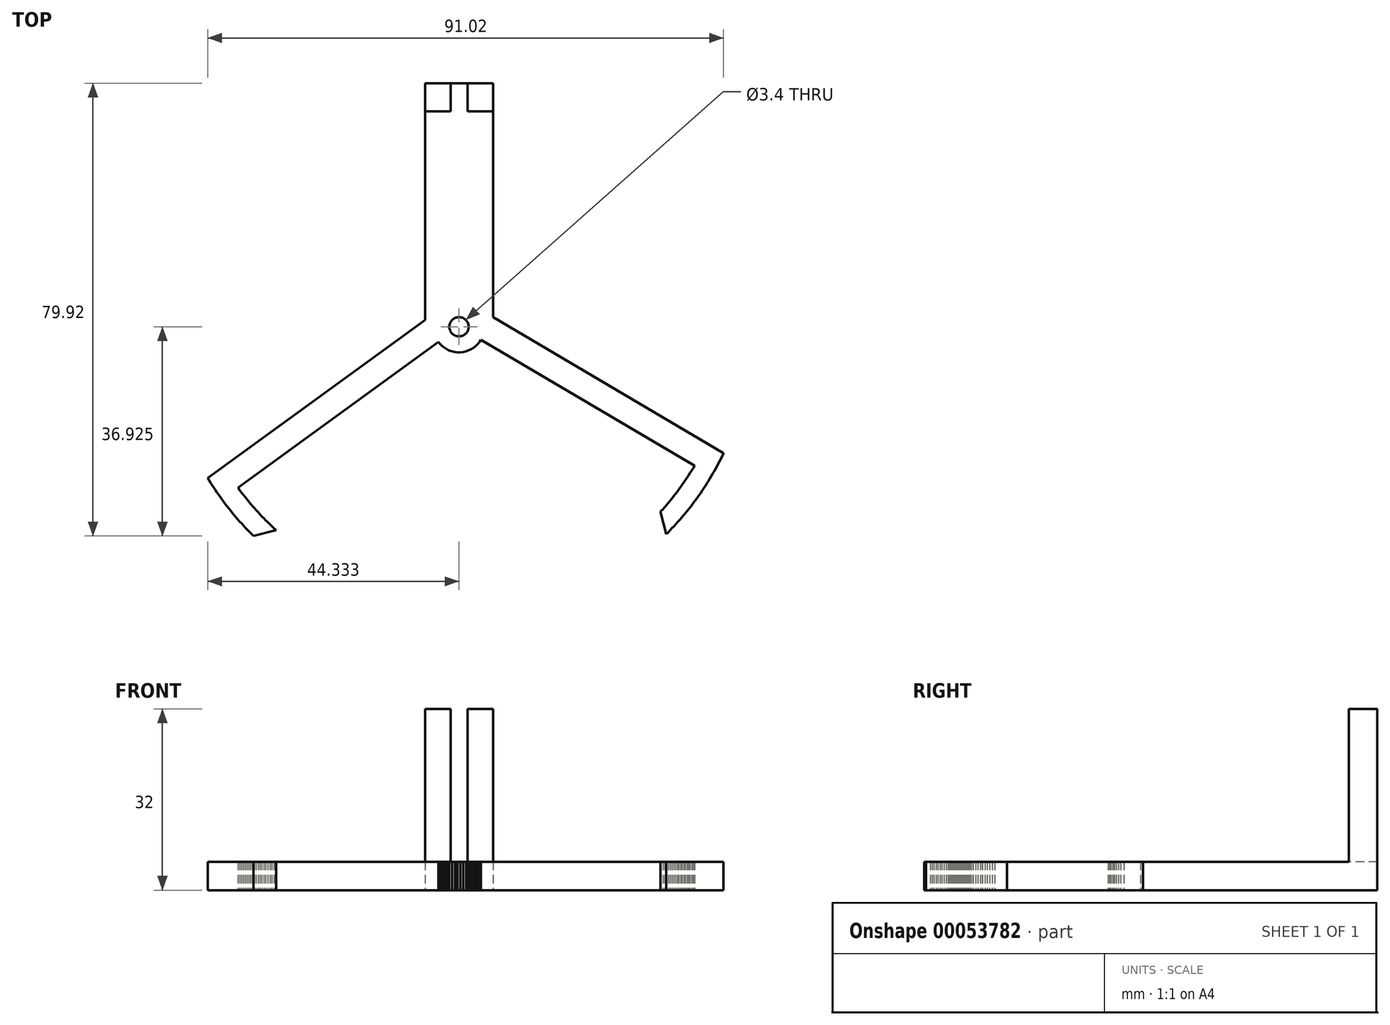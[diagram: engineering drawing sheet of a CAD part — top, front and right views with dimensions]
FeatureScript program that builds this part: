
annotation { "Feature Type Name" : "Feature", "Feature Type Description" : "" }
export const myFeature = defineFeature(function(context is Context, id is Id, definition is map)
    precondition{}
    {
        {
            var Q0;
            Q0=qCreatedBy(makeId("Top.planeOp"),FACE);
            var sketch = newSketch(context, id + "F0", { "sketchPlane" : qUnion([Q0])});
            skLineSegment(sketch, "E0", {"start": v(-33.44, -19.66) * mm, "end": v(-33.81, -19.33) * mm});
            skLineSegment(sketch, "E1", {"start": v(-33.81, -19.33) * mm, "end": v(-34.18, -18.99) * mm});
            skLineSegment(sketch, "E2", {"start": v(-34.18, -18.99) * mm, "end": v(-34.54, -18.64) * mm});
            skLineSegment(sketch, "E3", {"start": v(-34.54, -18.64) * mm, "end": v(-34.9, -18.3) * mm});
            skLineSegment(sketch, "E4", {"start": v(-34.9, -18.3) * mm, "end": v(-35.26, -17.95) * mm});
            skLineSegment(sketch, "E5", {"start": v(-35.26, -17.95) * mm, "end": v(-35.61, -17.6) * mm});
            skLineSegment(sketch, "E6", {"start": v(-35.61, -17.6) * mm, "end": v(-35.96, -17.23) * mm});
            skLineSegment(sketch, "E7", {"start": v(-35.96, -17.23) * mm, "end": v(-36.3, -16.87) * mm});
            skLineSegment(sketch, "E8", {"start": v(-36.3, -16.87) * mm, "end": v(-36.65, -16.5) * mm});
            skLineSegment(sketch, "E9", {"start": v(-36.65, -16.5) * mm, "end": v(-36.98, -16.13) * mm});
            skLineSegment(sketch, "E10", {"start": v(-36.98, -16.13) * mm, "end": v(-37.32, -15.76) * mm});
            skLineSegment(sketch, "E11", {"start": v(-37.32, -15.76) * mm, "end": v(-37.65, -15.39) * mm});
            skLineSegment(sketch, "E12", {"start": v(-37.65, -15.39) * mm, "end": v(-37.97, -15) * mm});
            skLineSegment(sketch, "E13", {"start": v(-37.97, -15) * mm, "end": v(-38.3, -14.62) * mm});
            skLineSegment(sketch, "E14", {"start": v(-38.3, -14.62) * mm, "end": v(-38.6, -14.24) * mm});
            skLineSegment(sketch, "E15", {"start": v(-38.6, -14.24) * mm, "end": v(-38.92, -13.85) * mm});
            skLineSegment(sketch, "E16", {"start": v(-38.92, -13.85) * mm, "end": v(-39.23, -13.45) * mm});
            skLineSegment(sketch, "E17", {"start": v(-39.23, -13.45) * mm, "end": v(-39.54, -13.06) * mm});
            skLineSegment(sketch, "E18", {"start": v(-39.54, -13.06) * mm, "end": v(-39.84, -12.66) * mm});
            skLineSegment(sketch, "E19", {"start": v(-39.84, -12.66) * mm, "end": v(-40.14, -12.26) * mm});
            skLineSegment(sketch, "E20", {"start": v(-40.14, -12.26) * mm, "end": v(-40.2, -12.17) * mm});
            skLineSegment(sketch, "E21", {"start": v(-40.2, -12.17) * mm, "end": v(-4.82, 13.57) * mm});
            skLineSegment(sketch, "E22", {"start": v(-4.82, 13.57) * mm, "end": v(-4.5, 13.18) * mm});
            skLineSegment(sketch, "E23", {"start": v(-4.5, 13.18) * mm, "end": v(-4.14, 12.83) * mm});
            skLineSegment(sketch, "E24", {"start": v(-4.14, 12.83) * mm, "end": v(-3.75, 12.52) * mm});
            skLineSegment(sketch, "E25", {"start": v(-3.75, 12.52) * mm, "end": v(-3.32, 12.26) * mm});
            skLineSegment(sketch, "E26", {"start": v(-3.32, 12.26) * mm, "end": v(-2.87, 12.05) * mm});
            skLineSegment(sketch, "E27", {"start": v(-2.87, 12.05) * mm, "end": v(-2.4, 11.88) * mm});
            skLineSegment(sketch, "E28", {"start": v(-2.4, 11.88) * mm, "end": v(-1.91, 11.78) * mm});
            skLineSegment(sketch, "E29", {"start": v(-1.91, 11.78) * mm, "end": v(-1.42, 11.72) * mm});
            skLineSegment(sketch, "E30", {"start": v(-1.42, 11.72) * mm, "end": v(-0.92, 11.72) * mm});
            skLineSegment(sketch, "E31", {"start": v(-0.92, 11.72) * mm, "end": v(-0.42, 11.78) * mm});
            skLineSegment(sketch, "E32", {"start": v(-0.42, 11.78) * mm, "end": v(0.07, 11.9) * mm});
            skLineSegment(sketch, "E33", {"start": v(0.07, 11.9) * mm, "end": v(0.54, 12.06) * mm});
            skLineSegment(sketch, "E34", {"start": v(0.54, 12.06) * mm, "end": v(1, 12.27) * mm});
            skLineSegment(sketch, "E35", {"start": v(1, 12.27) * mm, "end": v(1.41, 12.54) * mm});
            skLineSegment(sketch, "E36", {"start": v(1.41, 12.54) * mm, "end": v(1.8, 12.85) * mm});
            skLineSegment(sketch, "E37", {"start": v(1.8, 12.85) * mm, "end": v(2.16, 13.2) * mm});
            skLineSegment(sketch, "E38", {"start": v(2.16, 13.2) * mm, "end": v(2.48, 13.59) * mm});
            skLineSegment(sketch, "E39", {"start": v(2.48, 13.59) * mm, "end": v(2.7, 13.93) * mm});
            skLineSegment(sketch, "E40", {"start": v(2.7, 13.93) * mm, "end": v(40.39, -8.3) * mm});
            skLineSegment(sketch, "E41", {"start": v(40.39, -8.3) * mm, "end": v(40.13, -8.73) * mm});
            skLineSegment(sketch, "E42", {"start": v(40.13, -8.73) * mm, "end": v(39.87, -9.16) * mm});
            skLineSegment(sketch, "E43", {"start": v(39.87, -9.16) * mm, "end": v(39.6, -9.58) * mm});
            skLineSegment(sketch, "E44", {"start": v(39.6, -9.58) * mm, "end": v(39.34, -10) * mm});
            skLineSegment(sketch, "E45", {"start": v(39.34, -10) * mm, "end": v(39.06, -10.42) * mm});
            skLineSegment(sketch, "E46", {"start": v(39.06, -10.42) * mm, "end": v(38.78, -10.84) * mm});
            skLineSegment(sketch, "E47", {"start": v(38.78, -10.84) * mm, "end": v(38.5, -11.25) * mm});
            skLineSegment(sketch, "E48", {"start": v(38.5, -11.25) * mm, "end": v(38.21, -11.66) * mm});
            skLineSegment(sketch, "E49", {"start": v(38.21, -11.66) * mm, "end": v(37.92, -12.06) * mm});
            skLineSegment(sketch, "E50", {"start": v(37.92, -12.06) * mm, "end": v(37.63, -12.47) * mm});
            skLineSegment(sketch, "E51", {"start": v(37.63, -12.47) * mm, "end": v(37.33, -12.87) * mm});
            skLineSegment(sketch, "E52", {"start": v(37.33, -12.87) * mm, "end": v(37.03, -13.27) * mm});
            skLineSegment(sketch, "E53", {"start": v(37.03, -13.27) * mm, "end": v(36.72, -13.66) * mm});
            skLineSegment(sketch, "E54", {"start": v(36.72, -13.66) * mm, "end": v(36.4, -14.05) * mm});
            skLineSegment(sketch, "E55", {"start": v(36.4, -14.05) * mm, "end": v(36.1, -14.44) * mm});
            skLineSegment(sketch, "E56", {"start": v(36.1, -14.44) * mm, "end": v(35.77, -14.82) * mm});
            skLineSegment(sketch, "E57", {"start": v(35.77, -14.82) * mm, "end": v(35.45, -15.2) * mm});
            skLineSegment(sketch, "E58", {"start": v(35.45, -15.2) * mm, "end": v(35.12, -15.58) * mm});
            skLineSegment(sketch, "E59", {"start": v(35.12, -15.58) * mm, "end": v(34.79, -15.96) * mm});
            skLineSegment(sketch, "E60", {"start": v(34.79, -15.96) * mm, "end": v(34.45, -16.33) * mm});
            skLineSegment(sketch, "E61", {"start": v(34.45, -16.33) * mm, "end": v(34.38, -16.4) * mm});
            skLineSegment(sketch, "E62", {"start": v(34.38, -16.4) * mm, "end": v(35.4, -20.4) * mm});
            skLineSegment(sketch, "E63", {"start": v(35.4, -20.4) * mm, "end": v(35.74, -20.04) * mm});
            skLineSegment(sketch, "E64", {"start": v(35.74, -20.04) * mm, "end": v(36.1, -19.68) * mm});
            skLineSegment(sketch, "E65", {"start": v(36.1, -19.68) * mm, "end": v(36.44, -19.32) * mm});
            skLineSegment(sketch, "E66", {"start": v(36.44, -19.32) * mm, "end": v(36.78, -18.96) * mm});
            skLineSegment(sketch, "E67", {"start": v(36.78, -18.96) * mm, "end": v(37.12, -18.59) * mm});
            skLineSegment(sketch, "E68", {"start": v(37.12, -18.59) * mm, "end": v(37.45, -18.22) * mm});
            skLineSegment(sketch, "E69", {"start": v(37.45, -18.22) * mm, "end": v(37.78, -17.84) * mm});
            skLineSegment(sketch, "E70", {"start": v(37.78, -17.84) * mm, "end": v(38.1, -17.46) * mm});
            skLineSegment(sketch, "E71", {"start": v(38.1, -17.46) * mm, "end": v(38.43, -17.08) * mm});
            skLineSegment(sketch, "E72", {"start": v(38.43, -17.08) * mm, "end": v(38.75, -16.7) * mm});
            skLineSegment(sketch, "E73", {"start": v(38.75, -16.7) * mm, "end": v(39.07, -16.3) * mm});
            skLineSegment(sketch, "E74", {"start": v(39.07, -16.3) * mm, "end": v(39.38, -15.92) * mm});
            skLineSegment(sketch, "E75", {"start": v(39.38, -15.92) * mm, "end": v(39.69, -15.53) * mm});
            skLineSegment(sketch, "E76", {"start": v(39.69, -15.53) * mm, "end": v(40, -15.13) * mm});
            skLineSegment(sketch, "E77", {"start": v(40, -15.13) * mm, "end": v(40.3, -14.73) * mm});
            skLineSegment(sketch, "E78", {"start": v(40.3, -14.73) * mm, "end": v(40.6, -14.33) * mm});
            skLineSegment(sketch, "E79", {"start": v(40.6, -14.33) * mm, "end": v(40.89, -13.92) * mm});
            skLineSegment(sketch, "E80", {"start": v(40.89, -13.92) * mm, "end": v(41.17, -13.52) * mm});
            skLineSegment(sketch, "E81", {"start": v(41.17, -13.52) * mm, "end": v(41.46, -13.1) * mm});
            skLineSegment(sketch, "E82", {"start": v(41.46, -13.1) * mm, "end": v(41.74, -12.7) * mm});
            skLineSegment(sketch, "E83", {"start": v(41.74, -12.7) * mm, "end": v(42.02, -12.28) * mm});
            skLineSegment(sketch, "E84", {"start": v(42.02, -12.28) * mm, "end": v(42.3, -11.86) * mm});
            skLineSegment(sketch, "E85", {"start": v(42.3, -11.86) * mm, "end": v(42.56, -11.44) * mm});
            skLineSegment(sketch, "E86", {"start": v(42.56, -11.44) * mm, "end": v(42.83, -11.01) * mm});
            skLineSegment(sketch, "E87", {"start": v(42.83, -11.01) * mm, "end": v(43.09, -10.58) * mm});
            skLineSegment(sketch, "E88", {"start": v(43.09, -10.58) * mm, "end": v(43.34, -10.16) * mm});
            skLineSegment(sketch, "E89", {"start": v(43.34, -10.16) * mm, "end": v(43.6, -9.72) * mm});
            skLineSegment(sketch, "E90", {"start": v(43.6, -9.72) * mm, "end": v(43.85, -9.3) * mm});
            skLineSegment(sketch, "E91", {"start": v(43.85, -9.3) * mm, "end": v(44.09, -8.85) * mm});
            skLineSegment(sketch, "E92", {"start": v(44.09, -8.85) * mm, "end": v(44.33, -8.42) * mm});
            skLineSegment(sketch, "E93", {"start": v(44.33, -8.42) * mm, "end": v(44.57, -7.98) * mm});
            skLineSegment(sketch, "E94", {"start": v(44.57, -7.98) * mm, "end": v(44.8, -7.53) * mm});
            skLineSegment(sketch, "E95", {"start": v(44.8, -7.53) * mm, "end": v(45.02, -7.09) * mm});
            skLineSegment(sketch, "E96", {"start": v(45.02, -7.09) * mm, "end": v(45.25, -6.64) * mm});
            skLineSegment(sketch, "E97", {"start": v(45.25, -6.64) * mm, "end": v(45.47, -6.19) * mm});
            skLineSegment(sketch, "E98", {"start": v(45.47, -6.19) * mm, "end": v(45.51, -6.1) * mm});
            skLineSegment(sketch, "E99", {"start": v(45.51, -6.1) * mm, "end": v(1.1, 20.1) * mm});
            skLineSegment(sketch, "E100", {"start": v(1.1, 20.1) * mm, "end": v(0.67, 20.32) * mm});
            skLineSegment(sketch, "E101", {"start": v(0.67, 20.32) * mm, "end": v(0.2, 20.5) * mm});
            skLineSegment(sketch, "E102", {"start": v(0.2, 20.5) * mm, "end": v(-0.28, 20.63) * mm});
            skLineSegment(sketch, "E103", {"start": v(-0.28, 20.63) * mm, "end": v(-0.78, 20.7) * mm});
            skLineSegment(sketch, "E104", {"start": v(-0.78, 20.7) * mm, "end": v(-1.28, 20.71) * mm});
            skLineSegment(sketch, "E105", {"start": v(-1.28, 20.71) * mm, "end": v(-1.78, 20.67) * mm});
            skLineSegment(sketch, "E106", {"start": v(-1.78, 20.67) * mm, "end": v(-2.27, 20.58) * mm});
            skLineSegment(sketch, "E107", {"start": v(-2.27, 20.58) * mm, "end": v(-2.75, 20.43) * mm});
            skLineSegment(sketch, "E108", {"start": v(-2.75, 20.43) * mm, "end": v(-3.2, 20.23) * mm});
            skLineSegment(sketch, "E109", {"start": v(-3.2, 20.23) * mm, "end": v(-3.64, 19.98) * mm});
            skLineSegment(sketch, "E110", {"start": v(-3.64, 19.98) * mm, "end": v(-3.82, 19.85) * mm});
            skLineSegment(sketch, "E111", {"start": v(-3.82, 19.85) * mm, "end": v(-45.51, -10.47) * mm});
            skLineSegment(sketch, "E112", {"start": v(-45.51, -10.47) * mm, "end": v(-45.25, -10.9) * mm});
            skLineSegment(sketch, "E113", {"start": v(-45.25, -10.9) * mm, "end": v(-44.99, -11.32) * mm});
            skLineSegment(sketch, "E114", {"start": v(-44.99, -11.32) * mm, "end": v(-44.72, -11.74) * mm});
            skLineSegment(sketch, "E115", {"start": v(-44.72, -11.74) * mm, "end": v(-44.45, -12.16) * mm});
            skLineSegment(sketch, "E116", {"start": v(-44.45, -12.16) * mm, "end": v(-44.17, -12.58) * mm});
            skLineSegment(sketch, "E117", {"start": v(-44.17, -12.58) * mm, "end": v(-43.89, -13) * mm});
            skLineSegment(sketch, "E118", {"start": v(-43.89, -13) * mm, "end": v(-43.6, -13.4) * mm});
            skLineSegment(sketch, "E119", {"start": v(-43.6, -13.4) * mm, "end": v(-43.32, -13.81) * mm});
            skLineSegment(sketch, "E120", {"start": v(-43.32, -13.81) * mm, "end": v(-43.02, -14.22) * mm});
            skLineSegment(sketch, "E121", {"start": v(-43.02, -14.22) * mm, "end": v(-42.73, -14.62) * mm});
            skLineSegment(sketch, "E122", {"start": v(-42.73, -14.62) * mm, "end": v(-42.43, -15.02) * mm});
            skLineSegment(sketch, "E123", {"start": v(-42.43, -15.02) * mm, "end": v(-42.13, -15.42) * mm});
            skLineSegment(sketch, "E124", {"start": v(-42.13, -15.42) * mm, "end": v(-41.82, -15.81) * mm});
            skLineSegment(sketch, "E125", {"start": v(-41.82, -15.81) * mm, "end": v(-41.5, -16.2) * mm});
            skLineSegment(sketch, "E126", {"start": v(-41.5, -16.2) * mm, "end": v(-41.2, -16.6) * mm});
            skLineSegment(sketch, "E127", {"start": v(-41.2, -16.6) * mm, "end": v(-40.87, -16.98) * mm});
            skLineSegment(sketch, "E128", {"start": v(-40.87, -16.98) * mm, "end": v(-40.55, -17.36) * mm});
            skLineSegment(sketch, "E129", {"start": v(-40.55, -17.36) * mm, "end": v(-40.22, -17.74) * mm});
            skLineSegment(sketch, "E130", {"start": v(-40.22, -17.74) * mm, "end": v(-39.9, -18.12) * mm});
            skLineSegment(sketch, "E131", {"start": v(-39.9, -18.12) * mm, "end": v(-39.56, -18.49) * mm});
            skLineSegment(sketch, "E132", {"start": v(-39.56, -18.49) * mm, "end": v(-39.22, -18.86) * mm});
            skLineSegment(sketch, "E133", {"start": v(-39.22, -18.86) * mm, "end": v(-38.88, -19.22) * mm});
            skLineSegment(sketch, "E134", {"start": v(-38.88, -19.22) * mm, "end": v(-38.54, -19.59) * mm});
            skLineSegment(sketch, "E135", {"start": v(-38.54, -19.59) * mm, "end": v(-38.2, -19.95) * mm});
            skLineSegment(sketch, "E136", {"start": v(-38.2, -19.95) * mm, "end": v(-37.84, -20.3) * mm});
            skLineSegment(sketch, "E137", {"start": v(-37.84, -20.3) * mm, "end": v(-37.48, -20.65) * mm});
            skLineSegment(sketch, "E138", {"start": v(-37.48, -20.65) * mm, "end": v(-37.42, -20.71) * mm});
            skLineSegment(sketch, "E139", {"start": v(-37.42, -20.71) * mm, "end": v(-33.44, -19.66) * mm});
            skCircle(sketch, "E140", {"center": v(-1.18, 16.21) * mm, "radius": 1.7 * mm});
            skPoint(sketch, "E141", {"position": v(-7.24, 17.37) * mm});
            skLineSegment(sketch, "E142", {"start": v(-2.68, 59.21) * mm, "end": v(-2.68, 54.21) * mm});
            skLineSegment(sketch, "E143", {"start": v(0.32, 59.21) * mm, "end": v(0.32, 54.21) * mm});
            skLineSegment(sketch, "E144", {"start": v(-7.18, 59.21) * mm, "end": v(4.82, 59.21) * mm});
            skLineSegment(sketch, "E145", {"start": v(-7.18, 54.21) * mm, "end": v(4.82, 54.21) * mm});
            skLineSegment(sketch, "E146", {"start": v(4.82, 13.73) * mm, "end": v(4.82, 59.21) * mm});
            skLineSegment(sketch, "E147", {"start": v(-1.18, 59.21) * mm, "end": v(-1.18, 13.73) * mm, "construction": true});
            skLineSegment(sketch, "E148", {"start": v(-7.18, 13.73) * mm, "end": v(-7.18, 59.21) * mm});
            skCircle(sketch, "E149", {"center": v(-1.18, 16.21) * mm, "radius": 4 * mm});
            skLineSegment(sketch, "E150", {"start": v(-7.18, 16.21) * mm, "end": v(4.82, 16.21) * mm, "construction": true});
            skLineSegment(sketch, "E151", {"start": v(-7.18, 13.73) * mm, "end": v(4.82, 13.73) * mm});
            skSolve(sketch);
        }
        {
            var Q0;
            Q0=makeQuery(id+"F0.imprint","IMPRINT",FACE,{"disambiguationData":[TD([[makeQuery(id+"F0.imprint","IMPRINT",EDGE,{"derivedFrom":sQuery(id+"F0.wireOp",EDGE,"E0")}),1.0]])]});
            var Q1;
            {var subQ5=sQuery(id+"F0.wireOp",EDGE,"E40");Q1=makeQuery(id+"F0.imprint","IMPRINT",FACE,{"disambiguationData":[TD([[makeQuery(id+"F0.imprint","IMPRINT",EDGE,{"derivedFrom":subQ5}),1.0]])]});}
            var Q2;
            {var subQ4=sQuery(id+"F0.wireOp",EDGE,"E22");Q2=makeQuery(id+"F0.imprint","IMPRINT",FACE,{"disambiguationData":[TD([[makeQuery(id+"F0.imprint","IMPRINT",EDGE,{"derivedFrom":subQ4}),1.0]])]});}
            var Q3;
            {var subQ0=sQuery(id+"F0.wireOp",EDGE,"7Wl6hOCf-y8FN-YXAg-lJnB-ywVYcL8Pvd7c");Q3=makeQuery(id+"F0.imprint","IMPRINT",FACE,{"disambiguationData":[TD([[makeQuery(id+"F0.imprint","IMPRINT",EDGE,{"derivedFrom":subQ0}),1.0]])]});}
            var Q4;
            {var subQ7=sQuery(id+"F0.wireOp",EDGE,"E100");Q4=makeQuery(id+"F0.imprint","IMPRINT",FACE,{"disambiguationData":[TD([[makeQuery(id+"F0.imprint","IMPRINT",EDGE,{"derivedFrom":subQ7}),-1.0]])]});}
            var Q5;
            {var subQ0=sQuery(id+"F0.wireOp",EDGE,"E100");Q5=makeQuery(id+"F0.imprint","IMPRINT",FACE,{"disambiguationData":[TD([[makeQuery(id+"F0.imprint","IMPRINT",EDGE,{"derivedFrom":subQ0}),1.0]])]});}
            var Q6;
            Q6=makeQuery(id+"F0.imprint","IMPRINT",FACE,{"disambiguationData":[TD([[makeQuery(id+"F0.imprint","IMPRINT",EDGE,{"derivedFrom":sQuery(id+"F0.wireOp",EDGE,"E0")}),1.0]])]});
            var Q7;
            Q7=makeQuery(id+"F0.imprint","IMPRINT",FACE,{"disambiguationData":[TD([[makeQuery(id+"F0.imprint","IMPRINT",EDGE,{"derivedFrom":sQuery(id+"F0.wireOp",EDGE,"E140")}),-1.0]])]});
            var Q8;
            {var subQ0=sQuery(id+"F0.wireOp",EDGE,"gpeoCXvY-1RkU-sdRD-Jcin-rU8xiW87tctx");var subQ1=sQuery(id+"F0.wireOp",EDGE,"ac43ed41-176c-43a0-8963-aafd62ddca72");var subQ2=makeQuery(id+"F0.imprint","INTERSECT",VERTEX,{"disambiguationData":[OD(0.0)],"derivedFrom":[subQ1,subQ0]});Q8=makeQuery(id+"F0.imprint","IMPRINT",FACE,{"disambiguationData":[TD([[makeQuery(id+"F0.imprint","IMPRINT",EDGE,{"disambiguationData":[TD([[subQ2,-1.0]])],"derivedFrom":subQ1}),1.0]])]});}
            var Q9;
            {var subQ0=sQuery(id+"F0.wireOp",EDGE,"E41");Q9=makeQuery(id+"F0.imprint","IMPRINT",FACE,{"disambiguationData":[TD([[makeQuery(id+"F0.imprint","IMPRINT",EDGE,{"derivedFrom":subQ0}),1.0]])]});}
            var Q10;
            {var subQ0=sQuery(id+"F0.wireOp",EDGE,"E151");var subQ1=sQuery(id+"F0.wireOp",EDGE,"E149");var subQ2=makeQuery(id+"F0.imprint","INTERSECT",VERTEX,{"disambiguationData":[OD(0.0)],"derivedFrom":[subQ1,subQ0]});Q10=makeQuery(id+"F0.imprint","IMPRINT",FACE,{"disambiguationData":[TD([[makeQuery(id+"F0.imprint","IMPRINT",EDGE,{"disambiguationData":[TD([[subQ2,-1.0]])],"derivedFrom":subQ1}),1.0]])]});}
            var Q11;
            Q11=makeQuery(id+"F0.imprint","IMPRINT",FACE,{"disambiguationData":[TD([[makeQuery(id+"F0.imprint","IMPRINT",EDGE,{"derivedFrom":sQuery(id+"F0.wireOp",EDGE,"a5ee5e0a-0ed0-45e9-a193-4ad686f830aa")}),-1.0]])]});
            var Q12;
            {var subQ0=sQuery(id+"F0.wireOp",EDGE,"E142");Q12=makeQuery(id+"F0.imprint","IMPRINT",FACE,{"disambiguationData":[TD([[makeQuery(id+"F0.imprint","IMPRINT",EDGE,{"derivedFrom":subQ0}),1.0]])]});}
            extrude(context, id + "F1", {"entities" : qUnion([Q0, Q1, Q2, Q3, Q4, Q5, Q6, Q7, Q8, Q9, Q10, Q11, Q12]), "depth" : 5 * mm});
        }
        {
            var Q0;
            {var subQ0=sQuery(id+"F0.wireOp",EDGE,"E142");Q0=makeQuery(id+"F0.imprint","IMPRINT",FACE,{"disambiguationData":[TD([[makeQuery(id+"F0.imprint","IMPRINT",EDGE,{"derivedFrom":subQ0}),-1.0]])]});}
            var Q1;
            {var subQ0=sQuery(id+"F0.wireOp",EDGE,"E143");Q1=makeQuery(id+"F0.imprint","IMPRINT",FACE,{"disambiguationData":[TD([[makeQuery(id+"F0.imprint","IMPRINT",EDGE,{"derivedFrom":subQ0}),1.0]])]});}
            extrude(context, id + "F2", {"entities" : qUnion([Q0, Q1]), "operationType" : NewBodyOperationType.ADD, "depth" : 32 * mm});
        }
    });
